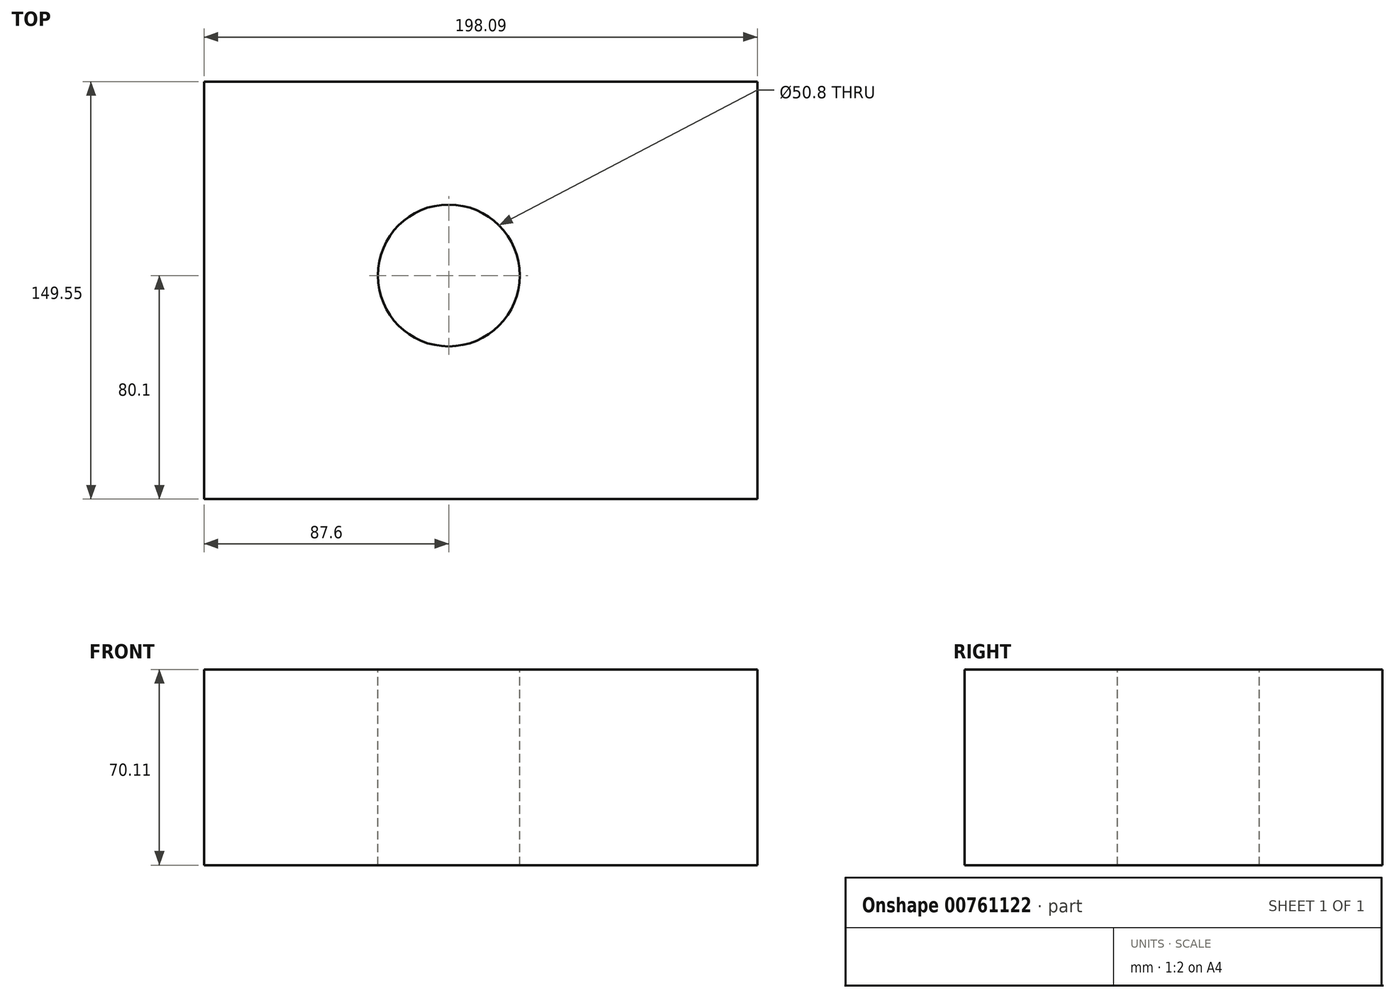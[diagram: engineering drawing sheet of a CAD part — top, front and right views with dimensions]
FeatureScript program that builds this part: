
annotation { "Feature Type Name" : "Feature", "Feature Type Description" : "" }
export const myFeature = defineFeature(function(context is Context, id is Id, definition is map)
    precondition{}
    {
        {
            var Q0;
            Q0=qCreatedBy(makeId("Top.planeOp"),FACE);
            var sketch = newSketch(context, id + "F0", { "sketchPlane" : qUnion([Q0])});
            skLineSegment(sketch, "E0.bottom", {"start": v(-87.6, 69.45) * mm, "end": v(110.49, 69.45) * mm});
            skLineSegment(sketch, "E0.top", {"start": v(-87.6, -80.1) * mm, "end": v(110.49, -80.1) * mm});
            skLineSegment(sketch, "E0.left", {"start": v(-87.6, 69.45) * mm, "end": v(-87.6, -80.1) * mm});
            skLineSegment(sketch, "E0.right", {"start": v(110.49, 69.45) * mm, "end": v(110.49, -80.1) * mm});
            skSolve(sketch);
        }
        {
            var Q0;
            Q0=makeQuery(id+"F0.imprint","IMPRINT",FACE,{"disambiguationData":[TD([[makeQuery(id+"F0.imprint","IMPRINT",EDGE,{"derivedFrom":sQuery(id+"F0.wireOp",EDGE,"E0.bottom")}),-1.0]])]});
            extrude(context, id + "F1", {"entities" : qUnion([Q0]), "depth" : 70.11 * mm, "offsetDistance" : 25.4 * mm});
        }
        {
            var Q0;
            Q0=makeQuery(id+"F1.opExtrude","CAP_FACE",FACE,{"disambiguationData":[OSD([sQuery(id+"F0.wireOp",EDGE,"E0.bottom"),sQuery(id+"F0.wireOp",EDGE,"E0.top"),sQuery(id+"F0.wireOp",EDGE,"E0.left"),sQuery(id+"F0.wireOp",EDGE,"E0.right")])],"isStart":false});
            var sketch = newSketch(context, id + "F2", { "sketchPlane" : qUnion([Q0])});
            skPoint(sketch, "E1", {"position": v(0, 0) * mm});
            skSolve(sketch);
        }
        {
            var Q0;
            Q0=sQuery(id+"F2.wireOp",VERTEX,"E1");
            var Q1;
            Q1=makeQuery(id+"F1.opExtrude","SWEPT_BODY",BODY,{"disambiguationData":[OSD([sQuery(id+"F0.wireOp",EDGE,"E0.bottom"),sQuery(id+"F0.wireOp",EDGE,"E0.top"),sQuery(id+"F0.wireOp",EDGE,"E0.left"),sQuery(id+"F0.wireOp",EDGE,"E0.right")])]});
            hole(context, id + "F3", {"style" : HoleStyle.SIMPLE, "endStyle" : HoleEndStyle.THROUGH, "holeDiameter" : 50.8 * mm, "majorDiameter" : 6.35 * mm, "isTappedThrough" : true, "tappedDepth" : 12.7 * mm, "tapClearance" : 3, "locations" : qUnion([Q0]), "scope" : qUnion([Q1])});
        }
    });
